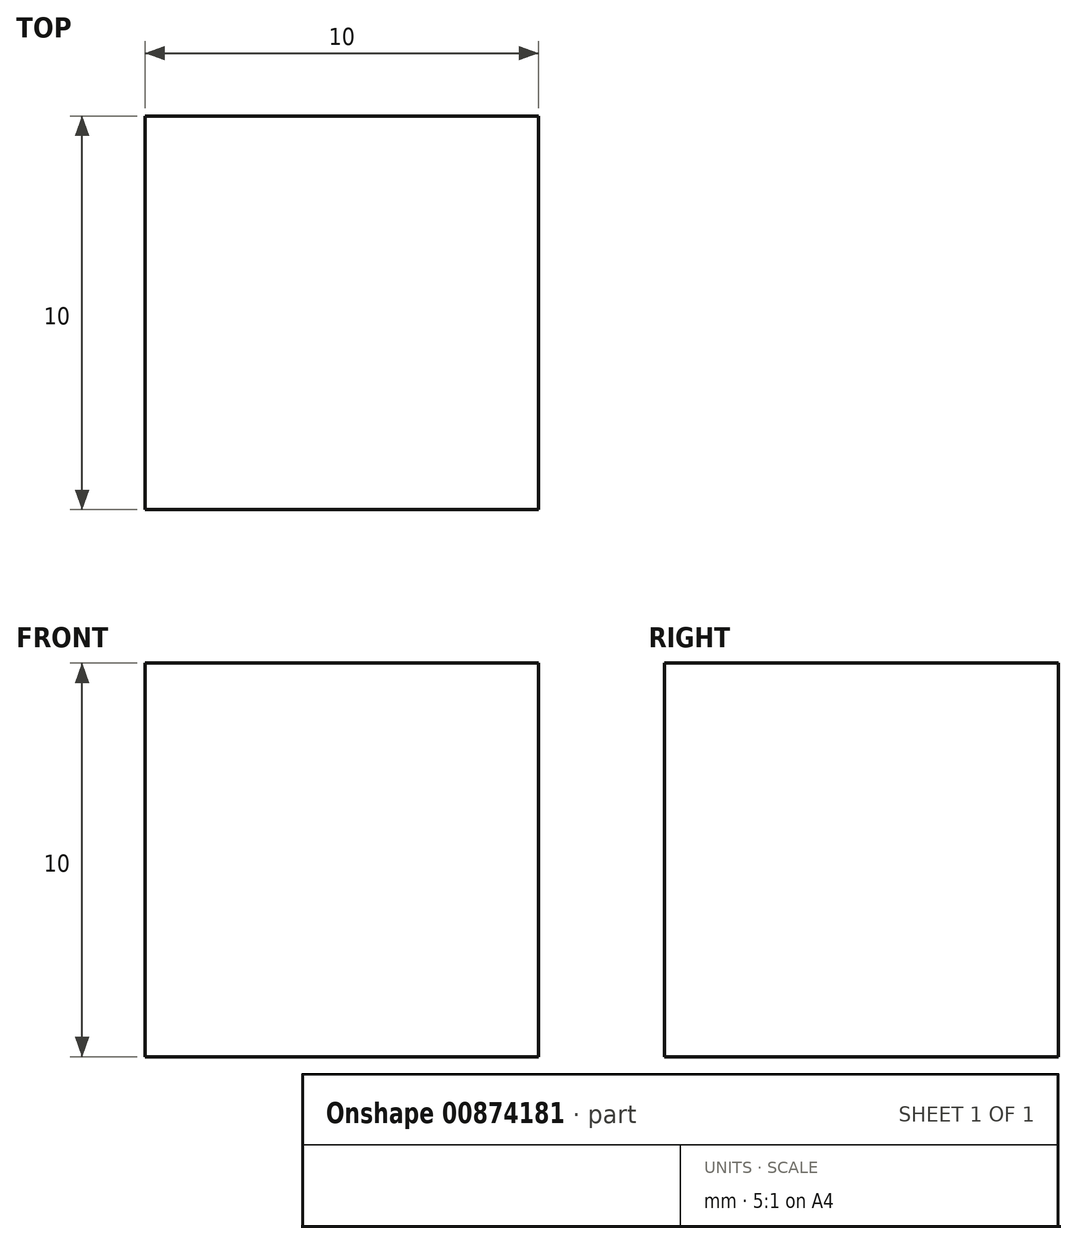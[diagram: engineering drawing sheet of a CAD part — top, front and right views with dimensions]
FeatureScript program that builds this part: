
annotation { "Feature Type Name" : "Feature", "Feature Type Description" : "" }
export const myFeature = defineFeature(function(context is Context, id is Id, definition is map)
    precondition{}
    {
        {
            var Q0;
            Q0=qCreatedBy(makeId("Front.planeOp"),FACE);
            var sketch = newSketch(context, id + "F0", { "sketchPlane" : qUnion([Q0])});
            skLineSegment(sketch, "E0.bottom", {"start": v(5, 5) * mm, "end": v(-5, 5) * mm});
            skLineSegment(sketch, "E0.top", {"start": v(5, -5) * mm, "end": v(-5, -5) * mm});
            skLineSegment(sketch, "E0.left", {"start": v(5, 5) * mm, "end": v(5, -5) * mm});
            skLineSegment(sketch, "E0.right", {"start": v(-5, 5) * mm, "end": v(-5, -5) * mm});
            skPoint(sketch, "E0.middle", {"position": v(0, 0) * mm});
            skSolve(sketch);
        }
        {
            var Q0;
            Q0=makeQuery(id+"F0.imprint","IMPRINT",FACE,{"disambiguationData":[TD([[makeQuery(id+"F0.imprint","IMPRINT",EDGE,{"derivedFrom":sQuery(id+"F0.wireOp",EDGE,"E0.bottom")}),1.0]])]});
            extrude(context, id + "F1", {"entities" : qUnion([Q0]), "depth" : 10 * mm, "offsetDistance" : 25 * mm});
        }
    });
